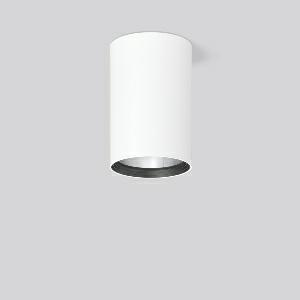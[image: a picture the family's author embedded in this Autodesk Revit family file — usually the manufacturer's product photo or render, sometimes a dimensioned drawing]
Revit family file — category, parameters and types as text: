
# Revit family: heledon_maxi_a_931226_002_2_76_d815
name_source: partatom
category: Lighting Fixtures
units: mm (PartAtom-declared; Revit-internal decimal feet)

## family parameters
Cut with Voids When Loaded = No
Host = Face
Light Source = No
Part Type = Normal
Room Calculation Point = No
Round Connector Dimension = Use Diameter
Shared = No

## types (1)
- HELEDON maxi A (1 x LED Modul 927, 3950 lm, 2700)
    Apparent Load = 35 VA
    Approval mark = CE
    CIE Flux Codes = 97 100 100 100 100
    Color Rendering = 92
    Color Temperature = 2700
    Default Elevation = 1800 mm
    Description = Series: HELEDON maxi
Cylindrical surface-mounted downlight. Housing: die-cast aluminium, powder-coated. Internal ceiling frame polycarbonate with bayonet mounting. Black plastic ring and recessed LED to prevent glare from the side. Optical assembly with reflector made of MIRO-Silver with 98% total light reflection for outstanding efficiency - can be changed without tools. Best colour rendering index Ra>90. Suitable for Ceiling mounting. Easy installation with a separate ceiling frame with bayonet mounting and plug connection. Driver integrated. Connected via plug-in connector. High quality converter without flickering and stroboscopic effect. The following accessories can be mounted without use of tools: interchangeable lenses, decorative glasses, honeycomb louvre, clear and frosted diffusers, white interchangeable plastic ring. 
Colour: traffic white, matt (RAL 9016)
Diameter: 123 mm
Height: 183 mm
Lamp: LED
Socket: without socket
Colour temperature: 2700K
Colour rendering index (CRI): 92
System power: 35 W
Rated luminous flux: 3950 lm
Luminous efficiency: 113 lm/W
Control gear: Converter, dimmable, DALI
Protection class: I
Type of protection: IP 20
    Height = 183 mm
    Lamp = 1 x LED Modul 927
    Lamp Light Flux = 3950 lm
    Lamp count = 1
    Length = 123 mm
    Lifetime = 50000 h
    Luminous efficacy = 113 lm/W
    Manufacturer = RZB
    ModVariant = No
    Model = 931226.002.2.76
    Mounting Place = Ceiling
    Mounting Type = Surface mounted
    Number of Poles = 1
    OnlyDefault = Yes
    Power Factor = 1
    Product Name = HELEDON maxi A
    Product group = Surface mounted downlights
    ProductGroupID = 302
    Protection Class = Protection class I
    Protection Degree = IP 20
    RLX_Detail_Level = 1
    RLX_Emergency_Light_Flux = 0 lm
    RLX_Emergency_Type = 0
    RLX_Emergency_Type_DB = No
    RlxData = <blob elided: 98785 chars, md5=39621349>
    Socket = socket
    Standby Power = 0 W
    System Light Flux = 3950 lm
    System Power = 35 W
    Type Comments = Product without accessories
    Type Image = 931192.002.jpg
    URL = http://relux.com
    VarID = ---
    Voltage = 230 V
    Voltage Range = 220-240 V
    Weight = 0.00 kg
    Width = 0 mm  [stored 0 ft]

note: [stored X ft] marks values corroborated as IEEE doubles in the binary element streams (Revit-internal decimal feet)

## geometry (parser evidence)
native form markers: Blend x4, Sweep x10
no freeform markers — native parametric forms only
